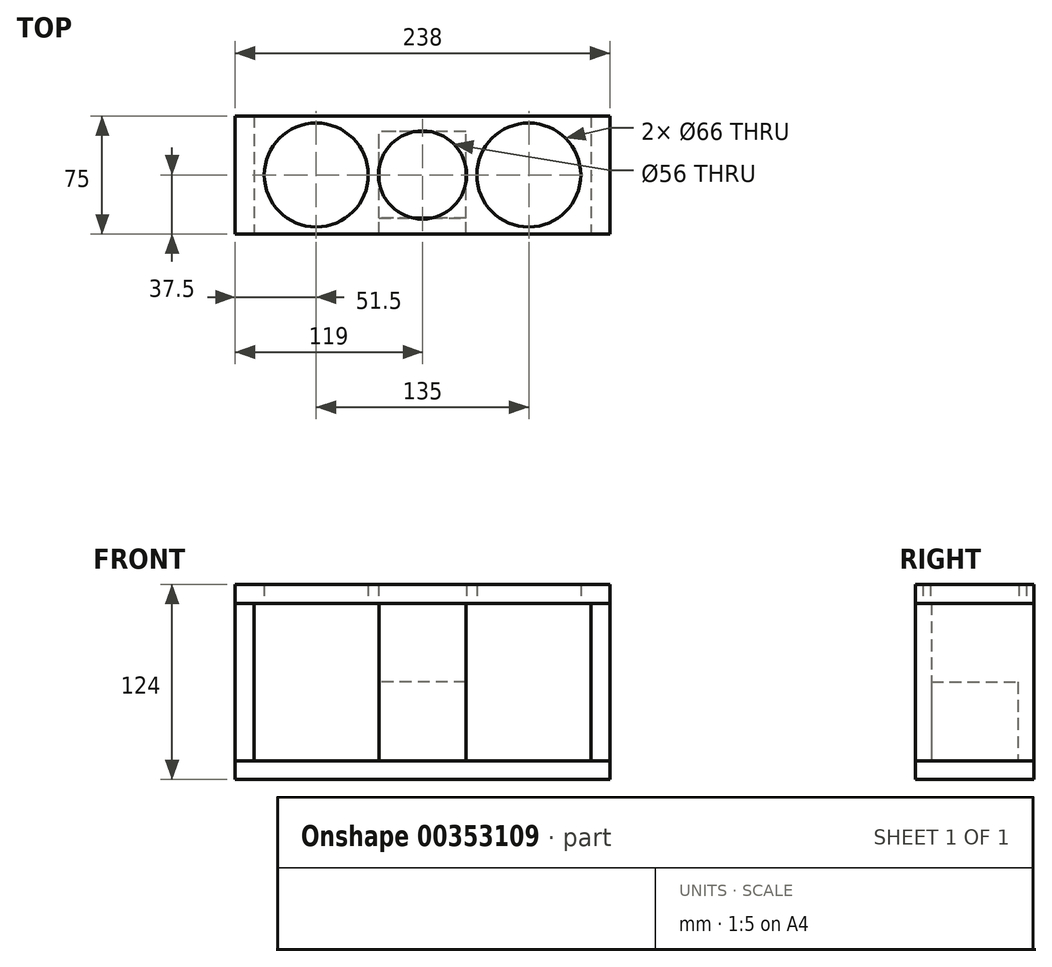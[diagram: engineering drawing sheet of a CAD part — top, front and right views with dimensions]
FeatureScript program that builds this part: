
annotation { "Feature Type Name" : "Feature", "Feature Type Description" : "" }
export const myFeature = defineFeature(function(context is Context, id is Id, definition is map)
    precondition{}
    {
        {
            var Q0;
            Q0=qCreatedBy(makeId("Top.planeOp"),FACE);
            var sketch = newSketch(context, id + "F0", { "sketchPlane" : qUnion([Q0])});
            skLineSegment(sketch, "E0.bottom", {"start": v(119, -37.5) * mm, "end": v(-119, -37.5) * mm});
            skLineSegment(sketch, "E0.top", {"start": v(119, 37.5) * mm, "end": v(-119, 37.5) * mm});
            skLineSegment(sketch, "E0.left", {"start": v(119, -37.5) * mm, "end": v(119, 37.5) * mm});
            skLineSegment(sketch, "E0.right", {"start": v(-119, -37.5) * mm, "end": v(-119, 37.5) * mm});
            skPoint(sketch, "E0.middle", {"position": v(0, 0) * mm});
            skSolve(sketch);
        }
        {
            var Q0;
            Q0=qSketchRegion(id+"F0",true);
            extrude(context, id + "F1", {"entities" : qUnion([Q0]), "depth" : 12 * mm});
        }
        {
            var Q0;
            Q0=makeQuery(id+"F1.opExtrude","CAP_FACE",FACE,{"disambiguationData":[OSD([sQuery(id+"F0.wireOp",EDGE,"E0.bottom"),sQuery(id+"F0.wireOp",EDGE,"E0.top"),sQuery(id+"F0.wireOp",EDGE,"E0.left"),sQuery(id+"F0.wireOp",EDGE,"E0.right")])],"isStart":false});
            cPlane(context, id + "F2", {"entities" : qUnion([Q0]), "cplaneType" : CPlaneType.OFFSET, "offset" : 100 * mm, "width" : 150 * mm, "height" : 150 * mm});
        }
        {
            var Q0;
            Q0=qCreatedBy(id+"F2.planeOp",FACE);
            var sketch = newSketch(context, id + "F3", { "sketchPlane" : qUnion([Q0])});
            skLineSegment(sketch, "E1.0", {"start": v(119, -37.5) * mm, "end": v(-119, -37.5) * mm});
            skLineSegment(sketch, "E1.1", {"start": v(119, 37.5) * mm, "end": v(-119, 37.5) * mm});
            skLineSegment(sketch, "E1.2", {"start": v(119, -37.5) * mm, "end": v(119, 37.5) * mm});
            skLineSegment(sketch, "E1.3", {"start": v(-119, -37.5) * mm, "end": v(-119, 37.5) * mm});
            skPoint(sketch, "E1.4", {"position": v(0, 0) * mm});
            skLineSegment(sketch, "E2", {"start": v(-119, 0) * mm, "end": v(119, 0) * mm, "construction": true});
            skCircle(sketch, "E3", {"center": v(-67.5, 0) * mm, "radius": 33 * mm});
            skLineSegment(sketch, "E4.direction1", {"start": v(-67.5, 0) * mm, "end": v(4.5, 0) * mm, "construction": true});
            skLineSegment(sketch, "E5", {"start": v(0, 0) * mm, "end": v(0, 37.5) * mm, "construction": true});
            skCircle(sketch, "E6.MirrorC", {"center": v(67.5, 0) * mm, "radius": 33 * mm});
            skCircle(sketch, "E7", {"center": v(0, 0) * mm, "radius": 28 * mm});
            skSolve(sketch);
        }
        {
            var Q0;
            Q0=qSketchRegion(id+"F3",true);
            extrude(context, id + "F4", {"entities" : qUnion([Q0]), "depth" : 12 * mm});
        }
        {
            var Q0;
            Q0=makeQuery(id+"F1.opExtrude","CAP_FACE",FACE,{"disambiguationData":[OSD([sQuery(id+"F0.wireOp",EDGE,"E0.bottom"),sQuery(id+"F0.wireOp",EDGE,"E0.top"),sQuery(id+"F0.wireOp",EDGE,"E0.left"),sQuery(id+"F0.wireOp",EDGE,"E0.right")])],"isStart":false});
            var sketch = newSketch(context, id + "F5", { "sketchPlane" : qUnion([Q0])});
            skLineSegment(sketch, "E8.bottom", {"start": v(-119, 37.5) * mm, "end": v(-107, 37.5) * mm});
            skLineSegment(sketch, "E8.top", {"start": v(-119, -37.5) * mm, "end": v(-107, -37.5) * mm});
            skLineSegment(sketch, "E8.left", {"start": v(-119, 37.5) * mm, "end": v(-119, -37.5) * mm});
            skLineSegment(sketch, "E8.right", {"start": v(-107, 37.5) * mm, "end": v(-107, -37.5) * mm});
            skLineSegment(sketch, "E9.bottom", {"start": v(119, 37.5) * mm, "end": v(107, 37.5) * mm});
            skLineSegment(sketch, "E9.top", {"start": v(119, -37.5) * mm, "end": v(107, -37.5) * mm});
            skLineSegment(sketch, "E9.left", {"start": v(119, 37.5) * mm, "end": v(119, -37.5) * mm});
            skLineSegment(sketch, "E9.right", {"start": v(107, 37.5) * mm, "end": v(107, -37.5) * mm});
            skSolve(sketch);
        }
        {
            var Q0;
            Q0=qSketchRegion(id+"F5",true);
            var Q1;
            Q1=qCreatedBy(id+"F2.planeOp",FACE);
            extrude(context, id + "F6", {"entities" : qUnion([Q0]), "endBound" : BoundingType.UP_TO_SURFACE, "endBoundEntityFace" : qUnion([Q1]), "depth" : 25 * mm});
        }
        {
            var Q0;
            Q0=makeQuery(id+"F1.opExtrude","CAP_FACE",FACE,{"disambiguationData":[OSD([sQuery(id+"F0.wireOp",EDGE,"E0.bottom"),sQuery(id+"F0.wireOp",EDGE,"E0.top"),sQuery(id+"F0.wireOp",EDGE,"E0.left"),sQuery(id+"F0.wireOp",EDGE,"E0.right")])],"isStart":false});
            var sketch = newSketch(context, id + "F7", { "sketchPlane" : qUnion([Q0])});
            skLineSegment(sketch, "E10.bottom", {"start": v(27.5, -27.5) * mm, "end": v(-27.5, -27.5) * mm});
            skLineSegment(sketch, "E10.top", {"start": v(27.5, 27.5) * mm, "end": v(-27.5, 27.5) * mm});
            skLineSegment(sketch, "E10.left", {"start": v(27.5, -27.5) * mm, "end": v(27.5, 27.5) * mm});
            skLineSegment(sketch, "E10.right", {"start": v(-27.5, -27.5) * mm, "end": v(-27.5, 27.5) * mm});
            skPoint(sketch, "E10.middle", {"position": v(0, 0) * mm});
            skSolve(sketch);
        }
        {
            var Q0;
            Q0 = qSketchRegion(id + "F7", true);
            extrude(context, id + "F8", {"entities" : qUnion([Q0]), "depth" : 50 * mm});
        }
        {
            var Q0;
            Q0=makeQuery(id+"F8.opExtrude","SWEPT_FACE",FACE,{"disambiguationData":[OSD([sQuery(id+"F7.wireOp",EDGE,"E10.bottom")])]});
            var sketch = newSketch(context, id + "F9", { "sketchPlane" : qUnion([Q0])});
            skLineSegment(sketch, "E11.bottom", {"start": v(-27.5, 12) * mm, "end": v(27.5, 12) * mm});
            skLineSegment(sketch, "E11.top", {"start": v(-27.5, 112) * mm, "end": v(27.5, 112) * mm});
            skLineSegment(sketch, "E11.left", {"start": v(-27.5, 12) * mm, "end": v(-27.5, 112) * mm});
            skLineSegment(sketch, "E11.right", {"start": v(27.5, 12) * mm, "end": v(27.5, 112) * mm});
            skSolve(sketch);
        }
        {
            var Q0;
            Q0 = qSketchRegion(id + "F9", true);
            extrude(context, id + "F10", {"entities" : qUnion([Q0]), "depth" : 10 * mm});
        }
    });
